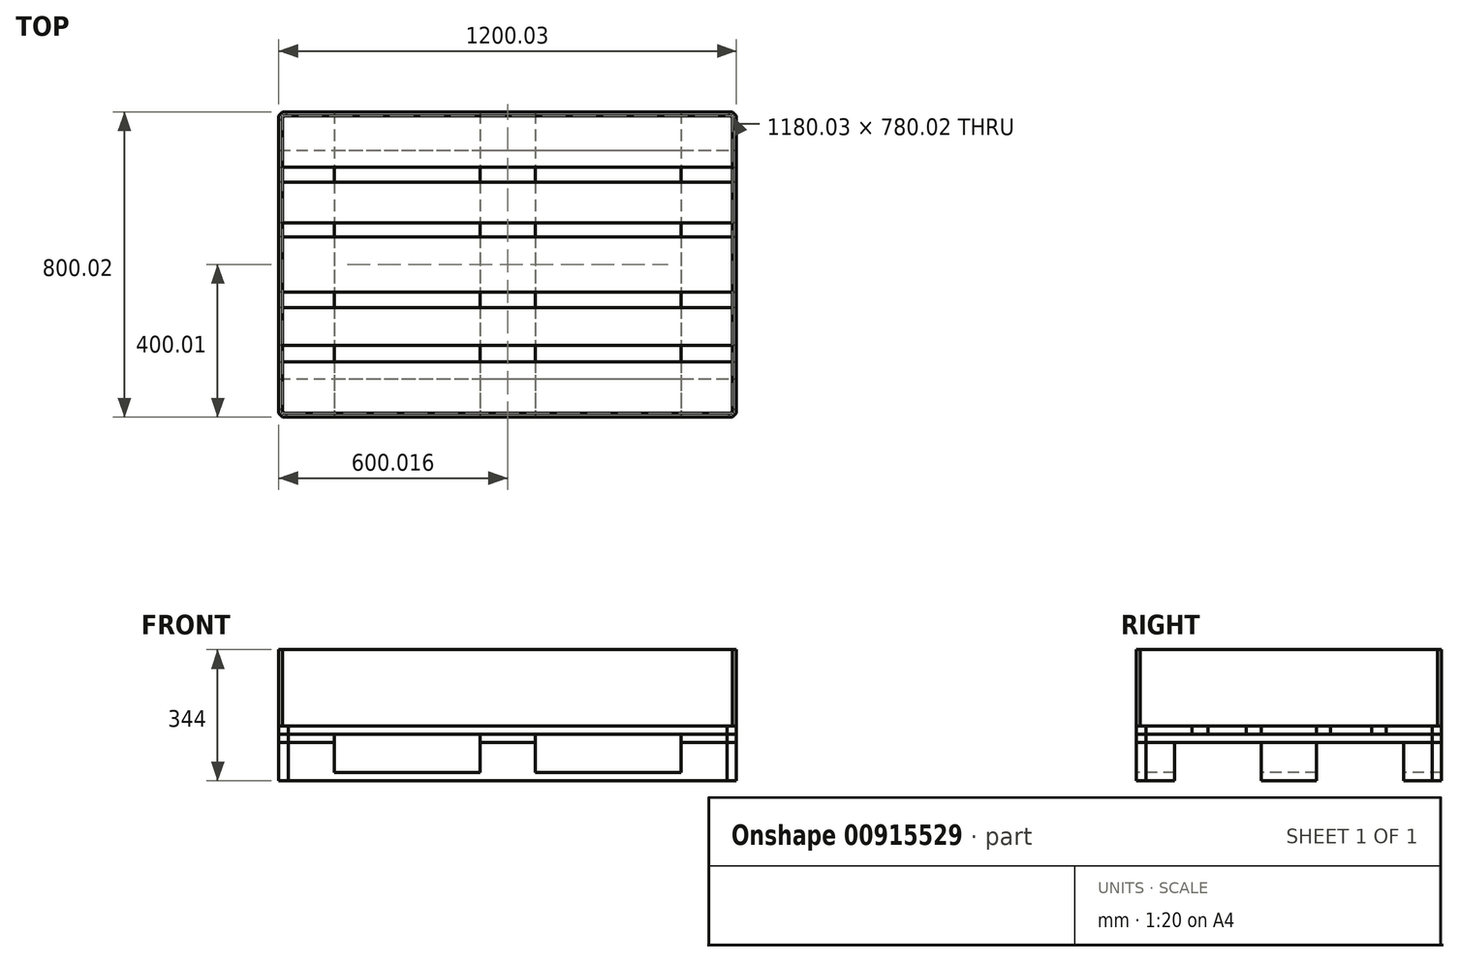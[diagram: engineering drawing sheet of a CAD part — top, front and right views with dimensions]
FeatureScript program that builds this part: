
annotation { "Feature Type Name" : "Feature", "Feature Type Description" : "" }
export const myFeature = defineFeature(function(context is Context, id is Id, definition is map)
    precondition{}
    {
        {
            var Q0;
            Q0=qCreatedBy(makeId("Top.planeOp"),FACE);
            var sketch = newSketch(context, id + "F0", { "sketchPlane" : qUnion([Q0])});
            skLineSegment(sketch, "E0.bottom", {"start": v(600, -400) * mm, "end": v(-600, -400) * mm});
            skLineSegment(sketch, "E0.top", {"start": v(600, 400) * mm, "end": v(-600, 400) * mm});
            skLineSegment(sketch, "E0.left", {"start": v(600, -400) * mm, "end": v(600, 400) * mm});
            skLineSegment(sketch, "E0.right", {"start": v(-600, -400) * mm, "end": v(-600, 400) * mm});
            skPoint(sketch, "E0.middle", {"position": v(0, 0) * mm});
            skLineSegment(sketch, "E1", {"start": v(-600, 300) * mm, "end": v(600, 300) * mm});
            skLineSegment(sketch, "E2", {"start": v(-600, -300) * mm, "end": v(600, -300) * mm});
            skLineSegment(sketch, "E3", {"start": v(-600, 0) * mm, "end": v(600, 0) * mm});
            skLineSegment(sketch, "E4", {"start": v(-600, 72.5) * mm, "end": v(600, 72.5) * mm});
            skLineSegment(sketch, "E5", {"start": v(-600, -72.5) * mm, "end": v(600, -72.5) * mm});
            skSolve(sketch);
        }
        {
            var Q0;
            {var subQ0=sQuery(id+"F0.wireOp",EDGE,"E0.top");Q0=makeQuery(id+"F0.imprint","IMPRINT",FACE,{"disambiguationData":[TD([[makeQuery(id+"F0.imprint","IMPRINT",EDGE,{"derivedFrom":subQ0}),1.0]])]});}
            var Q1;
            {var subQ0=sQuery(id+"F0.wireOp",EDGE,"E3");Q1=makeQuery(id+"F0.imprint","IMPRINT",FACE,{"disambiguationData":[TD([[makeQuery(id+"F0.imprint","IMPRINT",EDGE,{"derivedFrom":subQ0}),1.0]])]});}
            var Q2;
            {var subQ0=sQuery(id+"F0.wireOp",EDGE,"E3");Q2=makeQuery(id+"F0.imprint","IMPRINT",FACE,{"disambiguationData":[TD([[makeQuery(id+"F0.imprint","IMPRINT",EDGE,{"derivedFrom":subQ0}),-1.0]])]});}
            var Q3;
            {var subQ0=sQuery(id+"F0.wireOp",EDGE,"E0.bottom");Q3=makeQuery(id+"F0.imprint","IMPRINT",FACE,{"disambiguationData":[TD([[makeQuery(id+"F0.imprint","IMPRINT",EDGE,{"derivedFrom":subQ0}),-1.0]])]});}
            extrude(context, id + "F1", {"entities" : qUnion([Q0, Q1, Q2, Q3]), "depth" : 22 * mm});
        }
        {
            var Q0;
            Q0=makeQuery(id+"F1.opExtrude","CAP_FACE",FACE,{"disambiguationData":[OSD([sQuery(id+"F0.wireOp",EDGE,"E0.top"),sQuery(id+"F0.wireOp",EDGE,"E0.left"),sQuery(id+"F0.wireOp",EDGE,"E0.right"),sQuery(id+"F0.wireOp",EDGE,"E1")])],"isStart":false});
            var sketch = newSketch(context, id + "F2", { "sketchPlane" : qUnion([Q0])});
            skLineSegment(sketch, "E6", {"start": v(-455, 400) * mm, "end": v(-455, 300) * mm});
            skLineSegment(sketch, "E7", {"start": v(0, 400) * mm, "end": v(0, 300) * mm});
            skLineSegment(sketch, "E8", {"start": v(-72.5, 400) * mm, "end": v(-72.5, 300) * mm});
            skLineSegment(sketch, "E9", {"start": v(72.5, 400) * mm, "end": v(72.5, 300) * mm});
            skLineSegment(sketch, "E10", {"start": v(455, 400) * mm, "end": v(455, 300) * mm});
            skPoint(sketch, "E11.startSnap0", {"position": v(-455, 350) * mm});
            skSolve(sketch);
        }
        {
            var Q0;
            {var subQ0=sQuery(id+"F2.wireOp",EDGE,"E6");Q0=makeQuery(id+"F2.imprint","IMPRINT",FACE,{"disambiguationData":[TD([[makeQuery(id+"F2.imprint","IMPRINT",EDGE,{"derivedFrom":subQ0}),-1.0]])]});}
            var Q1;
            {var subQ0=sQuery(id+"F2.wireOp",EDGE,"E7");Q1=makeQuery(id+"F2.imprint","IMPRINT",FACE,{"disambiguationData":[TD([[makeQuery(id+"F2.imprint","IMPRINT",EDGE,{"derivedFrom":subQ0}),-1.0]])]});}
            var Q2;
            {var subQ0=sQuery(id+"F2.wireOp",EDGE,"E7");Q2=makeQuery(id+"F2.imprint","IMPRINT",FACE,{"disambiguationData":[TD([[makeQuery(id+"F2.imprint","IMPRINT",EDGE,{"derivedFrom":subQ0}),1.0]])]});}
            var Q3;
            {var subQ0=sQuery(id+"F2.wireOp",EDGE,"E10");Q3=makeQuery(id+"F2.imprint","IMPRINT",FACE,{"disambiguationData":[TD([[makeQuery(id+"F2.imprint","IMPRINT",EDGE,{"derivedFrom":subQ0}),1.0]])]});}
            extrude(context, id + "F3", {"entities" : qUnion([Q0, Q1, Q2, Q3]), "operationType" : NewBodyOperationType.ADD, "depth" : 78 * mm});
        }
        {
            var Q0;
            Q0=makeQuery(id+"F1.opExtrude","CAP_FACE",FACE,{"disambiguationData":[OSD([sQuery(id+"F0.wireOp",EDGE,"E0.left"),sQuery(id+"F0.wireOp",EDGE,"E0.right"),sQuery(id+"F0.wireOp",EDGE,"E4"),sQuery(id+"F0.wireOp",EDGE,"E5")])],"isStart":false});
            var sketch = newSketch(context, id + "F4", { "sketchPlane" : qUnion([Q0])});
            skLineSegment(sketch, "E12", {"start": v(-455, 72.5) * mm, "end": v(-455, -72.5) * mm});
            skLineSegment(sketch, "E13", {"start": v(-72.5, 72.5) * mm, "end": v(-72.5, -72.5) * mm});
            skLineSegment(sketch, "E14", {"start": v(72.5, 72.5) * mm, "end": v(72.5, -72.5) * mm});
            skLineSegment(sketch, "E15", {"start": v(455, 72.5) * mm, "end": v(455, -72.5) * mm});
            skSolve(sketch);
        }
        {
            var Q0;
            {var subQ0=sQuery(id+"F4.wireOp",EDGE,"E12");Q0=makeQuery(id+"F4.imprint","IMPRINT",FACE,{"disambiguationData":[TD([[makeQuery(id+"F4.imprint","IMPRINT",EDGE,{"derivedFrom":subQ0}),-1.0]])]});}
            var Q1;
            {var subQ0=sQuery(id+"F4.wireOp",EDGE,"E13");Q1=makeQuery(id+"F4.imprint","IMPRINT",FACE,{"disambiguationData":[TD([[makeQuery(id+"F4.imprint","IMPRINT",EDGE,{"derivedFrom":subQ0}),1.0]])]});}
            var Q2;
            {var subQ0=sQuery(id+"F4.wireOp",EDGE,"E15");Q2=makeQuery(id+"F4.imprint","IMPRINT",FACE,{"disambiguationData":[TD([[makeQuery(id+"F4.imprint","IMPRINT",EDGE,{"derivedFrom":subQ0}),1.0]])]});}
            extrude(context, id + "F5", {"entities" : qUnion([Q0, Q1, Q2]), "operationType" : NewBodyOperationType.ADD, "depth" : 78 * mm});
        }
        {
            var Q0;
            Q0=makeQuery(id+"F1.opExtrude","CAP_FACE",FACE,{"disambiguationData":[OSD([sQuery(id+"F0.wireOp",EDGE,"E0.bottom"),sQuery(id+"F0.wireOp",EDGE,"E0.left"),sQuery(id+"F0.wireOp",EDGE,"E0.right"),sQuery(id+"F0.wireOp",EDGE,"E2")])],"isStart":false});
            var sketch = newSketch(context, id + "F6", { "sketchPlane" : qUnion([Q0])});
            skLineSegment(sketch, "E16", {"start": v(-455, -300) * mm, "end": v(-455, -400) * mm});
            skLineSegment(sketch, "E17", {"start": v(-72.5, -300) * mm, "end": v(-72.5, -400) * mm});
            skLineSegment(sketch, "E18", {"start": v(72.5, -300) * mm, "end": v(72.5, -400) * mm});
            skLineSegment(sketch, "E19", {"start": v(455, -300) * mm, "end": v(455, -400) * mm});
            skSolve(sketch);
        }
        {
            var Q0;
            {var subQ0=sQuery(id+"F6.wireOp",EDGE,"E16");Q0=makeQuery(id+"F6.imprint","IMPRINT",FACE,{"disambiguationData":[TD([[makeQuery(id+"F6.imprint","IMPRINT",EDGE,{"derivedFrom":subQ0}),-1.0]])]});}
            var Q1;
            {var subQ0=sQuery(id+"F6.wireOp",EDGE,"E17");Q1=makeQuery(id+"F6.imprint","IMPRINT",FACE,{"disambiguationData":[TD([[makeQuery(id+"F6.imprint","IMPRINT",EDGE,{"derivedFrom":subQ0}),1.0]])]});}
            var Q2;
            {var subQ0=sQuery(id+"F6.wireOp",EDGE,"E19");Q2=makeQuery(id+"F6.imprint","IMPRINT",FACE,{"disambiguationData":[TD([[makeQuery(id+"F6.imprint","IMPRINT",EDGE,{"derivedFrom":subQ0}),1.0]])]});}
            extrude(context, id + "F7", {"entities" : qUnion([Q0, Q1, Q2]), "operationType" : NewBodyOperationType.ADD, "depth" : 78 * mm});
        }
        {
            var Q0;
            Q0=makeQuery(id+"F3.opExtrude","CAP_FACE",FACE,{"disambiguationData":[OSD([sQuery(id+"F0.wireOp",EDGE,"E0.top"),sQuery(id+"F0.wireOp",EDGE,"E0.right"),sQuery(id+"F0.wireOp",EDGE,"E1"),sQuery(id+"F2.wireOp",EDGE,"E6")])],"isStart":false});
            var sketch = newSketch(context, id + "F8", { "sketchPlane" : qUnion([Q0])});
            skLineSegment(sketch, "E20.bottom", {"start": v(-600, 400) * mm, "end": v(-455, 400) * mm});
            skLineSegment(sketch, "E20.top", {"start": v(-600, -400) * mm, "end": v(-455, -400) * mm});
            skLineSegment(sketch, "E20.left", {"start": v(-600, 400) * mm, "end": v(-600, -400) * mm});
            skLineSegment(sketch, "E20.right", {"start": v(-455, 400) * mm, "end": v(-455, -400) * mm});
            skSolve(sketch);
        }
        {
            var Q0;
            Q0=qSketchRegion(id+"F8",true);
            extrude(context, id + "F9", {"entities" : qUnion([Q0]), "depth" : 22 * mm});
        }
        {
            var Q0;
            Q0=makeQuery(id+"F3.opExtrude","CAP_FACE",FACE,{"disambiguationData":[OSD([sQuery(id+"F0.wireOp",EDGE,"E0.top"),sQuery(id+"F0.wireOp",EDGE,"E1"),sQuery(id+"F2.wireOp",EDGE,"E8"),sQuery(id+"F2.wireOp",EDGE,"E9")])],"isStart":false});
            var sketch = newSketch(context, id + "F10", { "sketchPlane" : qUnion([Q0])});
            skLineSegment(sketch, "E21.bottom", {"start": v(-72.5, 400) * mm, "end": v(72.5, 400) * mm});
            skLineSegment(sketch, "E21.top", {"start": v(-72.5, -400) * mm, "end": v(72.5, -400) * mm});
            skLineSegment(sketch, "E21.left", {"start": v(-72.5, 400) * mm, "end": v(-72.5, -400) * mm});
            skLineSegment(sketch, "E21.right", {"start": v(72.5, 400) * mm, "end": v(72.5, -400) * mm});
            skSolve(sketch);
        }
        {
            var Q0;
            Q0=qSketchRegion(id+"F10",true);
            extrude(context, id + "F11", {"entities" : qUnion([Q0]), "depth" : 22 * mm});
        }
        {
            var Q0;
            Q0=makeQuery(id+"F3.opExtrude","CAP_FACE",FACE,{"disambiguationData":[OSD([sQuery(id+"F0.wireOp",EDGE,"E0.top"),sQuery(id+"F0.wireOp",EDGE,"E0.left"),sQuery(id+"F0.wireOp",EDGE,"E1"),sQuery(id+"F2.wireOp",EDGE,"E10")])],"isStart":false});
            var sketch = newSketch(context, id + "F12", { "sketchPlane" : qUnion([Q0])});
            skLineSegment(sketch, "E22.bottom", {"start": v(455, 400) * mm, "end": v(600, 400) * mm});
            skLineSegment(sketch, "E22.top", {"start": v(455, -400) * mm, "end": v(600, -400) * mm});
            skLineSegment(sketch, "E22.left", {"start": v(455, 400) * mm, "end": v(455, -400) * mm});
            skLineSegment(sketch, "E22.right", {"start": v(600, 400) * mm, "end": v(600, -400) * mm});
            skSolve(sketch);
        }
        {
            var Q0;
            Q0=qSketchRegion(id+"F12",true);
            extrude(context, id + "F13", {"entities" : qUnion([Q0]), "depth" : 22 * mm});
        }
        {
            var Q0;
            Q0=makeQuery(id+"F9.opExtrude","CAP_FACE",FACE,{"disambiguationData":[OSD([sQuery(id+"F8.wireOp",EDGE,"E20.bottom"),sQuery(id+"F8.wireOp",EDGE,"E20.top"),sQuery(id+"F8.wireOp",EDGE,"E20.left"),sQuery(id+"F8.wireOp",EDGE,"E20.right")])],"isStart":false});
            var sketch = newSketch(context, id + "F14", { "sketchPlane" : qUnion([Q0])});
            skLineSegment(sketch, "E23.bottom", {"start": v(-600, 400) * mm, "end": v(600, 400) * mm});
            skLineSegment(sketch, "E23.top", {"start": v(-600, 255) * mm, "end": v(600, 255) * mm});
            skLineSegment(sketch, "E23.left", {"start": v(-600, 400) * mm, "end": v(-600, 255) * mm});
            skLineSegment(sketch, "E23.right", {"start": v(600, 400) * mm, "end": v(600, 255) * mm});
            skSolve(sketch);
        }
        {
            var Q0;
            Q0=qSketchRegion(id+"F14",true);
            extrude(context, id + "F15", {"entities" : qUnion([Q0]), "depth" : 22 * mm});
        }
        {
            var Q0;
            Q0=makeQuery(id+"F11.opExtrude","CAP_FACE",FACE,{"disambiguationData":[OSD([sQuery(id+"F10.wireOp",EDGE,"E21.bottom"),sQuery(id+"F10.wireOp",EDGE,"E21.top"),sQuery(id+"F10.wireOp",EDGE,"E21.left"),sQuery(id+"F10.wireOp",EDGE,"E21.right")])],"isStart":false});
            var sketch = newSketch(context, id + "F16", { "sketchPlane" : qUnion([Q0])});
            skLineSegment(sketch, "E24.bottom", {"start": v(600, 72.5) * mm, "end": v(-600, 72.5) * mm});
            skLineSegment(sketch, "E24.top", {"start": v(600, -72.5) * mm, "end": v(-600, -72.5) * mm});
            skLineSegment(sketch, "E24.left", {"start": v(600, 72.5) * mm, "end": v(600, -72.5) * mm});
            skLineSegment(sketch, "E24.right", {"start": v(-600, 72.5) * mm, "end": v(-600, -72.5) * mm});
            skPoint(sketch, "E24.middle", {"position": v(0, 0) * mm});
            skSolve(sketch);
        }
        {
            var Q0;
            Q0=qSketchRegion(id+"F16",true);
            extrude(context, id + "F17", {"entities" : qUnion([Q0]), "depth" : 22 * mm});
        }
        {
            var Q0;
            Q0=makeQuery(id+"F9.opExtrude","CAP_FACE",FACE,{"disambiguationData":[OSD([sQuery(id+"F8.wireOp",EDGE,"E20.bottom"),sQuery(id+"F8.wireOp",EDGE,"E20.top"),sQuery(id+"F8.wireOp",EDGE,"E20.left"),sQuery(id+"F8.wireOp",EDGE,"E20.right")])],"isStart":false});
            var sketch = newSketch(context, id + "F18", { "sketchPlane" : qUnion([Q0])});
            skLineSegment(sketch, "E25.bottom", {"start": v(-600, -400) * mm, "end": v(600, -400) * mm});
            skLineSegment(sketch, "E25.top", {"start": v(-600, -255) * mm, "end": v(600, -255) * mm});
            skLineSegment(sketch, "E25.left", {"start": v(-600, -400) * mm, "end": v(-600, -255) * mm});
            skLineSegment(sketch, "E25.right", {"start": v(600, -400) * mm, "end": v(600, -255) * mm});
            skSolve(sketch);
        }
        {
            var Q0;
            Q0=qSketchRegion(id+"F18",true);
            extrude(context, id + "F19", {"entities" : qUnion([Q0]), "depth" : 22 * mm});
        }
        {
            var Q0;
            Q0=makeQuery(id+"F9.opExtrude","CAP_FACE",FACE,{"disambiguationData":[OSD([sQuery(id+"F8.wireOp",EDGE,"E20.bottom"),sQuery(id+"F8.wireOp",EDGE,"E20.top"),sQuery(id+"F8.wireOp",EDGE,"E20.left"),sQuery(id+"F8.wireOp",EDGE,"E20.right")])],"isStart":false});
            var sketch = newSketch(context, id + "F20", { "sketchPlane" : qUnion([Q0])});
            skLineSegment(sketch, "E26.bottom", {"start": v(600, 108.92) * mm, "end": v(-600, 108.92) * mm});
            skLineSegment(sketch, "E26.top", {"start": v(600, 216.08) * mm, "end": v(-600, 216.08) * mm});
            skLineSegment(sketch, "E26.left", {"start": v(600, 108.92) * mm, "end": v(600, 216.08) * mm});
            skLineSegment(sketch, "E26.right", {"start": v(-600, 108.92) * mm, "end": v(-600, 216.08) * mm});
            skPoint(sketch, "E26.middle", {"position": v(0, 162.5) * mm});
            skSolve(sketch);
        }
        {
            var Q0;
            Q0=qSketchRegion(id+"F20",true);
            extrude(context, id + "F21", {"entities" : qUnion([Q0]), "depth" : 22 * mm});
        }
        {
            var Q0;
            Q0=makeQuery(id+"F9.opExtrude","CAP_FACE",FACE,{"disambiguationData":[OSD([sQuery(id+"F8.wireOp",EDGE,"E20.bottom"),sQuery(id+"F8.wireOp",EDGE,"E20.top"),sQuery(id+"F8.wireOp",EDGE,"E20.left"),sQuery(id+"F8.wireOp",EDGE,"E20.right")])],"isStart":false});
            var sketch = newSketch(context, id + "F22", { "sketchPlane" : qUnion([Q0])});
            skLineSegment(sketch, "E27.bottom", {"start": v(600, -112.5) * mm, "end": v(-600, -112.5) * mm});
            skLineSegment(sketch, "E27.top", {"start": v(600, -212.5) * mm, "end": v(-600, -212.5) * mm});
            skLineSegment(sketch, "E27.left", {"start": v(600, -112.5) * mm, "end": v(600, -212.5) * mm});
            skLineSegment(sketch, "E27.right", {"start": v(-600, -112.5) * mm, "end": v(-600, -212.5) * mm});
            skPoint(sketch, "E27.middle", {"position": v(0, -162.5) * mm});
            skSolve(sketch);
        }
        {
            var Q0;
            Q0=qSketchRegion(id+"F22",true);
            extrude(context, id + "F23", {"entities" : qUnion([Q0]), "depth" : 22 * mm});
        }
        {
            var Q0;
            Q0=makeQuery(id+"F19.opExtrude","SWEPT_EDGE",EDGE,{"disambiguationData":[OSD([sQuery(id+"F18.wireOp",EDGE,"E25.bottom"),sQuery(id+"F18.wireOp",EDGE,"E25.left")])]});
            var Q1;
            Q1=makeQuery(id+"F9.opExtrude","SWEPT_EDGE",EDGE,{"disambiguationData":[OSD([sQuery(id+"F8.wireOp",EDGE,"E20.top"),sQuery(id+"F8.wireOp",EDGE,"E20.left")])]});
            var Q2;
            {var subQ0=sQuery(id+"F0.wireOp",EDGE,"E0.right");var subQ1=sQuery(id+"F0.wireOp",EDGE,"E0.bottom");Q2=makeQuery(id+"F7.boolean.opBoolean","MERGE",EDGE,{"derivedFrom":[makeQuery(id+"F1.opExtrude","SWEPT_EDGE",EDGE,{"disambiguationData":[OSD([subQ1,subQ0])]}),makeQuery(id+"F7.opExtrude","SWEPT_EDGE",EDGE,{"disambiguationData":[OSD([subQ1,subQ0])]})]});}
            var Q3;
            Q3=makeQuery(id+"F19.opExtrude","SWEPT_EDGE",EDGE,{"disambiguationData":[OSD([sQuery(id+"F18.wireOp",EDGE,"E25.bottom"),sQuery(id+"F18.wireOp",EDGE,"E25.right")])]});
            var Q4;
            Q4=makeQuery(id+"F13.opExtrude","SWEPT_EDGE",EDGE,{"disambiguationData":[OSD([sQuery(id+"F12.wireOp",EDGE,"E22.top"),sQuery(id+"F12.wireOp",EDGE,"E22.right")])]});
            var Q5;
            {var subQ0=sQuery(id+"F0.wireOp",EDGE,"E0.left");var subQ1=sQuery(id+"F0.wireOp",EDGE,"E0.bottom");Q5=makeQuery(id+"F7.boolean.opBoolean","MERGE",EDGE,{"derivedFrom":[makeQuery(id+"F1.opExtrude","SWEPT_EDGE",EDGE,{"disambiguationData":[OSD([subQ1,subQ0])]}),makeQuery(id+"F7.opExtrude","SWEPT_EDGE",EDGE,{"disambiguationData":[OSD([subQ1,subQ0])]})]});}
            var Q6;
            Q6=makeQuery(id+"F15.opExtrude","SWEPT_EDGE",EDGE,{"disambiguationData":[OSD([sQuery(id+"F14.wireOp",EDGE,"E23.bottom"),sQuery(id+"F14.wireOp",EDGE,"E23.right")])]});
            var Q7;
            Q7=makeQuery(id+"F13.opExtrude","SWEPT_EDGE",EDGE,{"disambiguationData":[OSD([sQuery(id+"F12.wireOp",EDGE,"E22.bottom"),sQuery(id+"F12.wireOp",EDGE,"E22.right")])]});
            var Q8;
            {var subQ0=sQuery(id+"F0.wireOp",EDGE,"E0.left");var subQ1=sQuery(id+"F0.wireOp",EDGE,"E0.top");Q8=makeQuery(id+"F3.boolean.opBoolean","MERGE",EDGE,{"derivedFrom":[makeQuery(id+"F1.opExtrude","SWEPT_EDGE",EDGE,{"disambiguationData":[OSD([subQ1,subQ0])]}),makeQuery(id+"F3.opExtrude","SWEPT_EDGE",EDGE,{"disambiguationData":[OSD([subQ1,subQ0])]})]});}
            var Q9;
            Q9=makeQuery(id+"F15.opExtrude","SWEPT_EDGE",EDGE,{"disambiguationData":[OSD([sQuery(id+"F14.wireOp",EDGE,"E23.bottom"),sQuery(id+"F14.wireOp",EDGE,"E23.left")])]});
            var Q10;
            Q10=makeQuery(id+"F9.opExtrude","SWEPT_EDGE",EDGE,{"disambiguationData":[OSD([sQuery(id+"F8.wireOp",EDGE,"E20.bottom"),sQuery(id+"F8.wireOp",EDGE,"E20.left")])]});
            var Q11;
            {var subQ0=sQuery(id+"F0.wireOp",EDGE,"E0.right");var subQ1=sQuery(id+"F0.wireOp",EDGE,"E0.top");Q11=makeQuery(id+"F3.boolean.opBoolean","MERGE",EDGE,{"derivedFrom":[makeQuery(id+"F1.opExtrude","SWEPT_EDGE",EDGE,{"disambiguationData":[OSD([subQ1,subQ0])]}),makeQuery(id+"F3.opExtrude","SWEPT_EDGE",EDGE,{"disambiguationData":[OSD([subQ1,subQ0])]})]});}
            chamfer(context, id + "F24", {"entities" : qUnion([Q0, Q1, Q2, Q3, Q4, Q5, Q6, Q7, Q8, Q9, Q10, Q11]), "width" : 25 * mm, "tangentPropagation" : true});
        }
        {
            var Q0;
            Q0=makeQuery(id+"F15.opExtrude","CAP_FACE",FACE,{"disambiguationData":[OSD([sQuery(id+"F14.wireOp",EDGE,"E23.bottom"),sQuery(id+"F14.wireOp",EDGE,"E23.top"),sQuery(id+"F14.wireOp",EDGE,"E23.left"),sQuery(id+"F14.wireOp",EDGE,"E23.right")])],"isStart":false});
            var sketch = newSketch(context, id + "F25", { "sketchPlane" : qUnion([Q0])});
            skLineSegment(sketch, "E28.bottom", {"start": v(-600, 400) * mm, "end": v(600.03, 400) * mm});
            skLineSegment(sketch, "E28.top", {"start": v(-600, -400.02) * mm, "end": v(600.03, -400.02) * mm});
            skLineSegment(sketch, "E28.left", {"start": v(-600, 400) * mm, "end": v(-600, -400.02) * mm});
            skLineSegment(sketch, "E28.right", {"start": v(600.03, 400) * mm, "end": v(600.03, -400.02) * mm});
            skLineSegment(sketch, "E29.0", {"start": v(-590, 390) * mm, "end": v(590.03, 390) * mm});
            skLineSegment(sketch, "E29.1", {"start": v(-590, 390) * mm, "end": v(-590, -390.02) * mm});
            skLineSegment(sketch, "E29.2", {"start": v(-590, -390.02) * mm, "end": v(590.03, -390.02) * mm});
            skLineSegment(sketch, "E29.3", {"start": v(590.03, 390) * mm, "end": v(590.03, -390.02) * mm});
            skSolve(sketch);
        }
        {
            var Q0;
            {var subQ0=sQuery(id+"F25.wireOp",EDGE,"E28.bottom");var subQ1=sQuery(id+"F14.wireOp",EDGE,"E23.right");var subQ2=sQuery(id+"F14.wireOp",EDGE,"E23.left");var subQ3=sQuery(id+"F14.wireOp",EDGE,"E23.bottom");var subQ4=makeQuery(id+"F15.opExtrude","CAP_FACE",FACE,{"disambiguationData":[OSD([subQ3,sQuery(id+"F14.wireOp",EDGE,"E23.top"),subQ2,subQ1])],"isStart":false});var subQ5=makeQuery(id+"F24.opChamfer","BLEND_EDGE",EDGE,{"blendedFrom":[makeQuery(id+"F15.opExtrude","SWEPT_EDGE",EDGE,{"disambiguationData":[OSD([subQ3,subQ2])]}),subQ4],"blendedInto":[subQ4]});var subQ6=makeQuery(id+"F25.imprint","INTERSECT",VERTEX,{"derivedFrom":[subQ5,subQ0]});Q0=makeQuery(id+"F25.imprint","IMPRINT",FACE,{"disambiguationData":[TD([[makeQuery(id+"F25.imprint","IMPRINT",EDGE,{"disambiguationData":[TD([[subQ6,-1.0]])],"derivedFrom":subQ0}),-1.0]])]});}
            var Q1;
            {var subQ7=sQuery(id+"F25.wireOp",EDGE,"E28.left");var subQ9=sQuery(id+"F25.wireOp",EDGE,"E28.bottom");var subQ10=makeQuery(id+"F25.imprint","INTERSECT",VERTEX,{"derivedFrom":[subQ9,subQ7]});Q1=makeQuery(id+"F25.imprint","IMPRINT",FACE,{"disambiguationData":[TD([[makeQuery(id+"F25.imprint","IMPRINT",EDGE,{"disambiguationData":[TD([[subQ10,-1.0]])],"derivedFrom":subQ9}),-1.0]])]});}
            var Q2;
            {var subQ0=sQuery(id+"F25.wireOp",EDGE,"E28.left");var subQ1=sQuery(id+"F14.wireOp",EDGE,"E23.top");var subQ2=makeQuery(id+"F15.opExtrude","CAP_EDGE",EDGE,{"disambiguationData":[OSD([subQ1])],"isStart":false});var subQ3=makeQuery(id+"F25.imprint","INTERSECT",VERTEX,{"derivedFrom":[subQ2,subQ0]});Q2=makeQuery(id+"F25.imprint","IMPRINT",FACE,{"disambiguationData":[TD([[makeQuery(id+"F25.imprint","IMPRINT",EDGE,{"disambiguationData":[TD([[subQ3,-1.0]])],"derivedFrom":subQ2}),1.0]])]});}
            var Q3;
            {var subQ18=sQuery(id+"F25.wireOp",EDGE,"E28.top");Q3=makeQuery(id+"F25.imprint","IMPRINT",FACE,{"disambiguationData":[TD([[makeQuery(id+"F25.imprint","IMPRINT",EDGE,{"derivedFrom":subQ18}),1.0]])]});}
            var Q4;
            {var subQ1=sQuery(id+"F14.wireOp",EDGE,"E23.right");var subQ8=makeQuery(id+"F15.opExtrude","CAP_EDGE",EDGE,{"disambiguationData":[OSD([subQ1])],"isStart":false});Q4=makeQuery(id+"F25.imprint","IMPRINT",FACE,{"disambiguationData":[TD([[makeQuery(id+"F25.imprint","IMPRINT",EDGE,{"derivedFrom":subQ8}),-1.0]])]});}
            extrude(context, id + "F26", {"entities" : qUnion([Q0, Q1, Q2, Q3, Q4]), "depth" : 200 * mm, "offsetDistance" : 25 * mm});
        }
        {
            var Q0;
            Q0=makeQuery(id+"F26.opExtrude","SWEPT_EDGE",EDGE,{"disambiguationData":[OSD([sQuery(id+"F25.wireOp",EDGE,"E28.top"),sQuery(id+"F25.wireOp",EDGE,"E28.right")])]});
            var Q1;
            Q1=makeQuery(id+"F26.opExtrude","SWEPT_EDGE",EDGE,{"disambiguationData":[OSD([sQuery(id+"F25.wireOp",EDGE,"E28.bottom"),sQuery(id+"F25.wireOp",EDGE,"E28.right")])]});
            var Q2;
            Q2=makeQuery(id+"F26.opExtrude","SWEPT_EDGE",EDGE,{"disambiguationData":[OSD([sQuery(id+"F25.wireOp",EDGE,"E28.top"),sQuery(id+"F25.wireOp",EDGE,"E28.left")])]});
            var Q3;
            Q3=makeQuery(id+"F26.opExtrude","SWEPT_EDGE",EDGE,{"disambiguationData":[OSD([sQuery(id+"F25.wireOp",EDGE,"E28.bottom"),sQuery(id+"F25.wireOp",EDGE,"E28.left")])]});
            chamfer(context, id + "F27", {"entities" : qUnion([Q0, Q1, Q2, Q3]), "width" : 10 * mm, "tangentPropagation" : true});
        }
    });
